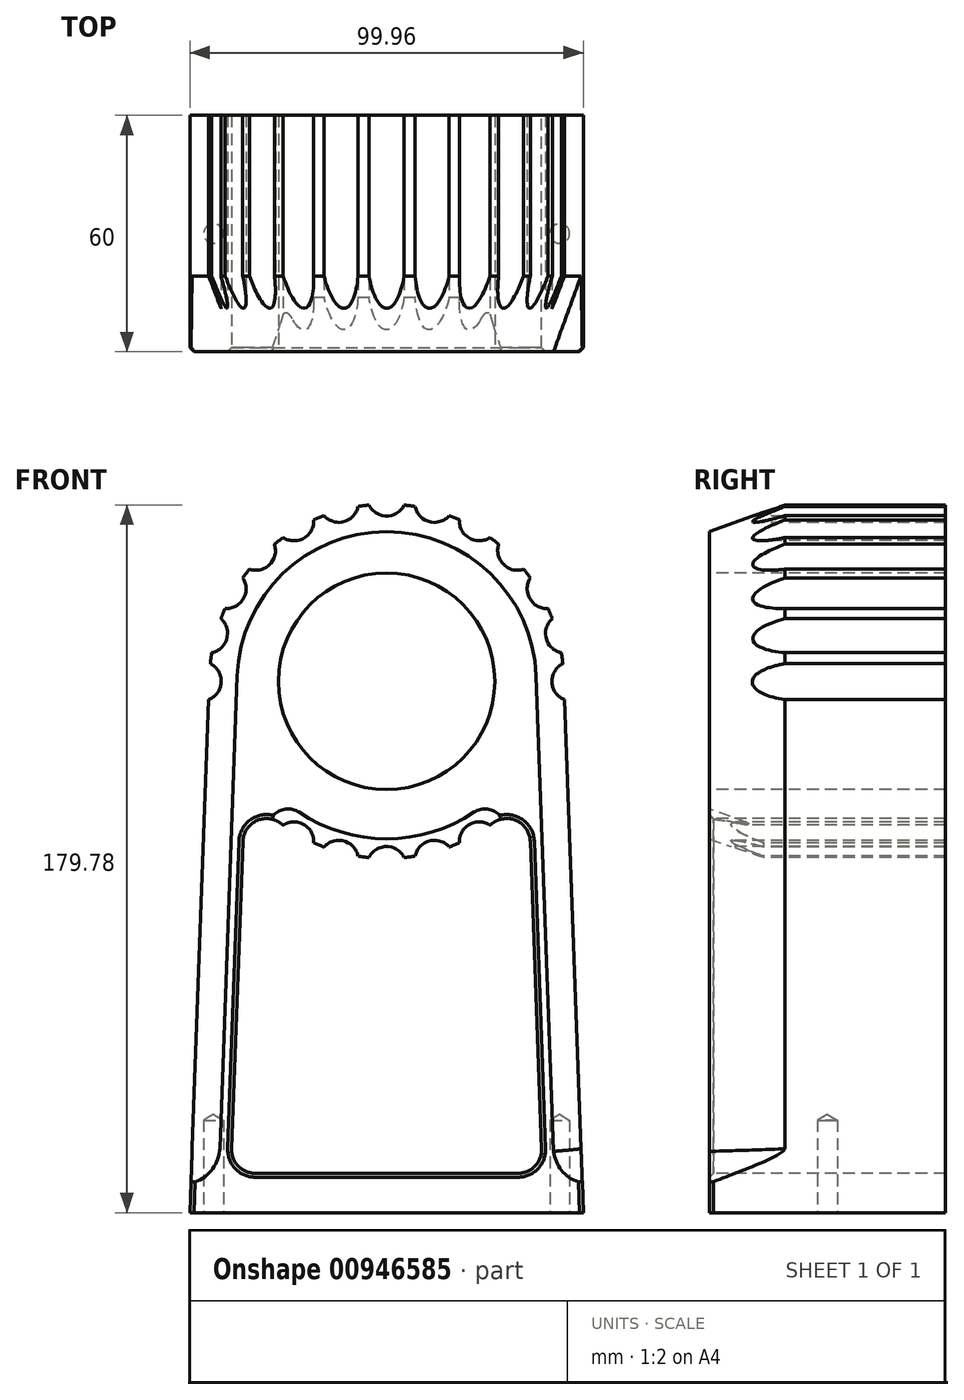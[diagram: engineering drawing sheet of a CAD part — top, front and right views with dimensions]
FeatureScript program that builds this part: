
annotation { "Feature Type Name" : "Feature", "Feature Type Description" : "" }
export const myFeature = defineFeature(function(context is Context, id is Id, definition is map)
    precondition{}
    {
        {
            var Q0;
            Q0=qCreatedBy(makeId("Front.planeOp"),FACE);
            var sketch = newSketch(context, id + "F0", { "sketchPlane" : qUnion([Q0])});
            skLineSegment(sketch, "E0.top", {"start": v(-50, -99.3) * mm, "end": v(-49.96, -99.3) * mm});
            skLineSegment(sketch, "E1", {"start": v(0, 121.96) * mm, "end": v(0, -115.93) * mm, "construction": true});
            skCircle(sketch, "E2", {"center": v(0, 35.7) * mm, "radius": 27.5 * mm});
            skLineSegment(sketch, "E3.trimOffspring", {"start": v(-39.59, -89.3) * mm, "end": v(39.63, -89.3) * mm});
            skPoint(sketch, "E4.orphan", {"position": v(-49.96, -99.3) * mm});
            skLineSegment(sketch, "E5", {"start": v(-68.26, 80.7) * mm, "end": v(50, 80.7) * mm, "construction": true});
            skLineSegment(sketch, "E6", {"start": v(50, 80.7) * mm, "end": v(50, -149.68) * mm, "construction": true});
            skArc(sketch, "E7", {"start": v(44.97, 37.36) * mm, "mid": v(0, 80.7) * mm, "end": v(-44.97, 37.34) * mm});
            skLineSegment(sketch, "E8", {"start": v(-49.96, -99.3) * mm, "end": v(-44.97, 37.34) * mm});
            skLineSegment(sketch, "E9", {"start": v(50, -99.3) * mm, "end": v(44.97, 37.36) * mm});
            skArc(sketch, "E10.trimOffspring", {"start": v(-36, 8.71) * mm, "mid": v(0, -9.3) * mm, "end": v(36.02, 8.72) * mm});
            skLineSegment(sketch, "E11.trimOffspring", {"start": v(39.63, -89.3) * mm, "end": v(36.02, 8.72) * mm});
            skLineSegment(sketch, "E12.trimOffspring", {"start": v(-39.59, -89.3) * mm, "end": v(-36, 8.71) * mm});
            skLineSegment(sketch, "E13.trimOffspring", {"start": v(-49.96, -99.3) * mm, "end": v(50, -99.3) * mm});
            skSolve(sketch);
        }
        {
            var Q0;
            Q0=qSketchRegion(id+"F0",true);
            extrude(context, id + "F1", {"entities" : qUnion([Q0]), "oppositeDirection" : true, "depth" : 60 * mm, "offsetDistance" : 25 * mm});
        }
        {
            var Q0;
            Q0=makeQuery(id+"F1.opExtrude","CAP_FACE",FACE,{"disambiguationData":[OSD([sQuery(id+"F0.wireOp",EDGE,"E2"),sQuery(id+"F0.wireOp",EDGE,"E3.trimOffspring"),sQuery(id+"F0.wireOp",EDGE,"E7"),sQuery(id+"F0.wireOp",EDGE,"E8"),sQuery(id+"F0.wireOp",EDGE,"E9"),sQuery(id+"F0.wireOp",EDGE,"E10.trimOffspring"),sQuery(id+"F0.wireOp",EDGE,"E11.trimOffspring"),sQuery(id+"F0.wireOp",EDGE,"E12.trimOffspring"),sQuery(id+"F0.wireOp",EDGE,"E13.trimOffspring")])],"isStart":true});
            var sketch = newSketch(context, id + "F2", { "sketchPlane" : qUnion([Q0])});
            skArc(sketch, "E14.0", {"start": v(44.97, 37.36) * mm, "mid": v(0, 80.7) * mm, "end": v(-44.97, 37.34) * mm, "construction": true});
            skArc(sketch, "E15.0", {"start": v(61.97, 55.33) * mm, "mid": v(0, 100.7) * mm, "end": v(-61.97, 55.33) * mm});
            skArc(sketch, "E16.0", {"start": v(37.97, 37.1) * mm, "mid": v(0, 73.7) * mm, "end": v(-37.97, 37.09) * mm});
            skArc(sketch, "E17.0", {"start": v(-36, 8.71) * mm, "mid": v(0, -9.3) * mm, "end": v(36.02, 8.72) * mm, "construction": true});
            skArc(sketch, "E18.0", {"start": v(-22.22, 2.44) * mm, "mid": v(0, -4.3) * mm, "end": v(22.22, 2.44) * mm});
            skArc(sketch, "E19.0", {"start": v(-21.86, -25.51) * mm, "mid": v(0.68, -29.3) * mm, "end": v(23.14, -25.04) * mm});
            skArc(sketch, "E20", {"start": v(-22.22, 2.44) * mm, "mid": v(-28.07, 2.23) * mm, "end": v(-29.71, -3.39) * mm});
            skArc(sketch, "E21", {"start": v(29.78, -3.17) * mm, "mid": v(27.98, 2.3) * mm, "end": v(22.22, 2.44) * mm});
            skLineSegment(sketch, "E22", {"start": v(-21.86, -25.51) * mm, "end": v(-29.71, -3.39) * mm});
            skLineSegment(sketch, "E23", {"start": v(23.14, -25.04) * mm, "end": v(29.78, -3.17) * mm});
            skLineSegment(sketch, "E24", {"start": v(0, 35.7) * mm, "end": v(0, -65.78) * mm, "construction": true});
            skLineSegment(sketch, "E25", {"start": v(-37.97, 37.09) * mm, "end": v(-42.36, -82.91) * mm});
            skLineSegment(sketch, "E26", {"start": v(37.97, 37.1) * mm, "end": v(42.42, -83.72) * mm});
            skArc(sketch, "E27", {"start": v(-49.69, -91.8) * mm, "mid": v(-44.52, -88.6) * mm, "end": v(-42.36, -82.91) * mm});
            skArc(sketch, "E28.MirrorCS", {"start": v(49.69, -91.8) * mm, "mid": v(44.78, -88.9) * mm, "end": v(42.42, -83.72) * mm});
            skLineSegment(sketch, "E29", {"start": v(-61.97, 55.33) * mm, "end": v(-94.94, -91.8) * mm});
            skLineSegment(sketch, "E30", {"start": v(-94.94, -91.8) * mm, "end": v(-49.69, -91.8) * mm});
            skLineSegment(sketch, "E31.MirrorCS", {"start": v(61.97, 55.33) * mm, "end": v(94.94, -91.8) * mm});
            skLineSegment(sketch, "E32.MirrorCS", {"start": v(94.94, -91.8) * mm, "end": v(49.69, -91.8) * mm});
            skSolve(sketch);
        }
        {
            var Q0;
            {var subQ0=sQuery(id+"F2.wireOp",EDGE,"E18.0");Q0=makeQuery(id+"F2.imprint","IMPRINT",FACE,{"disambiguationData":[TD([[makeQuery(id+"F2.imprint","IMPRINT",EDGE,{"derivedFrom":subQ0}),-1.0]])]});}
            var Q1;
            Q1=makeQuery(id+"F2.imprint","IMPRINT",FACE,{"disambiguationData":[TD([[makeQuery(id+"F2.imprint","IMPRINT",EDGE,{"derivedFrom":sQuery(id+"F2.wireOp",EDGE,"E19.0")}),1.0]])]});
            var Q2;
            Q2=makeQuery(id+"F2.imprint","IMPRINT",FACE,{"disambiguationData":[TD([[makeQuery(id+"F2.imprint","IMPRINT",EDGE,{"derivedFrom":sQuery(id+"F2.wireOp",EDGE,"E15.0")}),1.0]])]});
            var Q3;
            Q3=makeQuery(id+"F2.imprint","IMPRINT",FACE,{"disambiguationData":[TD([[makeQuery(id+"F2.imprint","IMPRINT",EDGE,{"derivedFrom":sQuery(id+"F2.wireOp",EDGE,"E16.0")}),-1.0]])]});
            extrude(context, id + "F3", {"entities" : qUnion([Q0, Q1, Q2, Q3]), "operationType" : NewBodyOperationType.REMOVE, "endBound" : BoundingType.THROUGH_ALL, "oppositeDirection" : true, "depth" : 25 * mm, "offsetDistance" : 25 * mm, "hasDraft" : true, "draftAngle" : 20 * degree, "draftPullDirection" : true});
        }
        {
            var Q0;
            Q0=makeQuery(id+"F1.opExtrude","SWEPT_EDGE",EDGE,{"disambiguationData":[OSD([sQuery(id+"F0.wireOp",EDGE,"E10.trimOffspring"),sQuery(id+"F0.wireOp",EDGE,"E12.trimOffspring")])]});
            var Q1;
            Q1=makeQuery(id+"F1.opExtrude","SWEPT_EDGE",EDGE,{"disambiguationData":[OSD([sQuery(id+"F0.wireOp",EDGE,"E10.trimOffspring"),sQuery(id+"F0.wireOp",EDGE,"E11.trimOffspring")])]});
            var Q2;
            Q2=makeQuery(id+"F1.opExtrude","SWEPT_EDGE",EDGE,{"disambiguationData":[OSD([sQuery(id+"F0.wireOp",EDGE,"E3.trimOffspring"),sQuery(id+"F0.wireOp",EDGE,"E12.trimOffspring")])]});
            var Q3;
            Q3=makeQuery(id+"F1.opExtrude","SWEPT_EDGE",EDGE,{"disambiguationData":[OSD([sQuery(id+"F0.wireOp",EDGE,"E3.trimOffspring"),sQuery(id+"F0.wireOp",EDGE,"E11.trimOffspring")])]});
            fillet(context, id + "F4", {"entities" : qUnion([Q0, Q1, Q2, Q3]), "radius" : 6 * mm, "tangentPropagation" : true, "allowEdgeOverflow" : false});
        }
        {
            var Q0;
            Q0=makeQuery(id+"F1.opExtrude","CAP_FACE",FACE,{"disambiguationData":[OSD([sQuery(id+"F0.wireOp",EDGE,"E2"),sQuery(id+"F0.wireOp",EDGE,"E3.trimOffspring"),sQuery(id+"F0.wireOp",EDGE,"E7"),sQuery(id+"F0.wireOp",EDGE,"E8"),sQuery(id+"F0.wireOp",EDGE,"E9"),sQuery(id+"F0.wireOp",EDGE,"E10.trimOffspring"),sQuery(id+"F0.wireOp",EDGE,"E11.trimOffspring"),sQuery(id+"F0.wireOp",EDGE,"E12.trimOffspring"),sQuery(id+"F0.wireOp",EDGE,"E13.trimOffspring")])],"isStart":true});
            var sketch = newSketch(context, id + "F5", { "sketchPlane" : qUnion([Q0])});
            skArc(sketch, "E33", {"start": v(-44.4, 42.96) * mm, "mid": v(-44.62, 41.58) * mm, "end": v(-44.78, 40.18) * mm});
            skLineSegment(sketch, "E34", {"start": v(0, 35.7) * mm, "end": v(0, 109) * mm, "construction": true});
            skPoint(sketch, "E35", {"position": v(0, 82.7) * mm});
            skLineSegment(sketch, "E36.anchor1", {"start": v(0, 35.7) * mm, "end": v(0, 82.7) * mm, "construction": true});
            skLineSegment(sketch, "E36.anchor2", {"start": v(0, 35.7) * mm, "end": v(0, 82.7) * mm, "construction": true});
            skArc(sketch, "E37", {"start": v(-4.48, 80.48) * mm, "mid": v(0, 77.7) * mm, "end": v(4.48, 80.48) * mm});
            skArc(sketch, "E38.1.0", {"start": v(-15.91, 77.8) * mm, "mid": v(-10.87, 76.27) * mm, "end": v(-7.26, 80.11) * mm});
            skArc(sketch, "E38.2.0", {"start": v(-26.27, 72.24) * mm, "mid": v(-21, 72.07) * mm, "end": v(-18.5, 76.72) * mm});
            skArc(sketch, "E38.3.0", {"start": v(-34.83, 64.2) * mm, "mid": v(-29.7, 65.4) * mm, "end": v(-28.5, 70.53) * mm});
            skArc(sketch, "E38.4.0", {"start": v(-41.02, 54.21) * mm, "mid": v(-36.37, 56.7) * mm, "end": v(-36.54, 61.97) * mm});
            skArc(sketch, "E38.5.0", {"start": v(-44.4, 42.96) * mm, "mid": v(-40.57, 46.57) * mm, "end": v(-42.1, 51.62) * mm});
            skArc(sketch, "E38.6.0", {"start": v(-46.73, 30.7) * mm, "mid": v(-42.1, 34.69) * mm, "end": v(-44.78, 40.18) * mm});
            skArc(sketch, "E38.10.0", {"start": v(-18.5, -5.32) * mm, "mid": v(-21.93, -0.26) * mm, "end": v(-27.7, -2.27) * mm});
            skArc(sketch, "E38.11.0", {"start": v(-7.26, -8.7) * mm, "mid": v(-10.87, -4.87) * mm, "end": v(-15.91, -6.4) * mm});
            skArc(sketch, "E38.12.0", {"start": v(4.48, -9.08) * mm, "mid": v(0, -6.3) * mm, "end": v(-4.48, -9.08) * mm});
            skArc(sketch, "E38.13.0", {"start": v(15.91, -6.4) * mm, "mid": v(10.87, -4.87) * mm, "end": v(7.26, -8.7) * mm});
            skArc(sketch, "E38.14.0", {"start": v(27.7, -2.27) * mm, "mid": v(21.93, -0.26) * mm, "end": v(18.5, -5.32) * mm});
            skArc(sketch, "E38.18.0", {"start": v(44.78, 40.18) * mm, "mid": v(42.1, 34.69) * mm, "end": v(46.73, 30.7) * mm});
            skArc(sketch, "E38.19.0", {"start": v(42.1, 51.62) * mm, "mid": v(40.57, 46.57) * mm, "end": v(44.4, 42.96) * mm});
            skArc(sketch, "E38.21.0", {"start": v(28.5, 70.53) * mm, "mid": v(29.7, 65.4) * mm, "end": v(34.83, 64.2) * mm});
            skArc(sketch, "E38.22.0", {"start": v(18.5, 76.72) * mm, "mid": v(21, 72.07) * mm, "end": v(26.27, 72.24) * mm});
            skArc(sketch, "E38.23.0", {"start": v(7.26, 80.11) * mm, "mid": v(10.87, 76.27) * mm, "end": v(15.91, 77.8) * mm});
            skArc(sketch, "E39", {"start": v(46.73, 30.7) * mm, "mid": v(0, 82.7) * mm, "end": v(-46.73, 30.7) * mm});
            skArc(sketch, "E40.trimOffspring", {"start": v(-41.02, 54.21) * mm, "mid": v(-41.57, 52.92) * mm, "end": v(-42.1, 51.62) * mm});
            skArc(sketch, "E41.trimOffspring", {"start": v(-34.83, 64.2) * mm, "mid": v(-35.7, 63.1) * mm, "end": v(-36.54, 61.97) * mm});
            skArc(sketch, "E42.trimOffspring", {"start": v(-26.27, 72.24) * mm, "mid": v(-27.4, 71.4) * mm, "end": v(-28.5, 70.53) * mm});
            skArc(sketch, "E43.trimOffspring", {"start": v(-15.91, 77.8) * mm, "mid": v(-17.22, 77.28) * mm, "end": v(-18.5, 76.72) * mm});
            skArc(sketch, "E44.trimOffspring", {"start": v(-4.48, 80.48) * mm, "mid": v(-5.87, 80.32) * mm, "end": v(-7.26, 80.11) * mm});
            skArc(sketch, "E45.trimOffspring", {"start": v(18.5, 76.72) * mm, "mid": v(11.65, 79.17) * mm, "end": v(4.48, 80.48) * mm});
            skArc(sketch, "E46.trimOffspring", {"start": v(28.5, 70.53) * mm, "mid": v(27.4, 71.4) * mm, "end": v(26.27, 72.24) * mm});
            skArc(sketch, "E47.trimOffspring", {"start": v(36.54, 61.97) * mm, "mid": v(35.7, 63.1) * mm, "end": v(34.83, 64.2) * mm});
            skArc(sketch, "E48.trimOffspring", {"start": v(42.1, 51.62) * mm, "mid": v(41.57, 52.92) * mm, "end": v(41.02, 54.21) * mm});
            skArc(sketch, "E49.trimOffspring", {"start": v(36.54, 61.97) * mm, "mid": v(36.37, 56.7) * mm, "end": v(41.02, 54.21) * mm});
            skArc(sketch, "E50.trimOffspring", {"start": v(44.78, 40.18) * mm, "mid": v(44.62, 41.58) * mm, "end": v(44.4, 42.96) * mm});
            skArc(sketch, "E51.trimOffspring", {"start": v(-27.7, -2.27) * mm, "mid": v(0, -11.3) * mm, "end": v(27.7, -2.27) * mm});
            skArc(sketch, "E52.trimOffspring", {"start": v(-18.5, -5.32) * mm, "mid": v(-17.22, -5.87) * mm, "end": v(-15.91, -6.4) * mm});
            skArc(sketch, "E53.trimOffspring", {"start": v(15.91, -6.4) * mm, "mid": v(17.22, -5.87) * mm, "end": v(18.5, -5.32) * mm});
            skArc(sketch, "E54.trimOffspring", {"start": v(4.48, -9.08) * mm, "mid": v(5.87, -8.91) * mm, "end": v(7.26, -8.7) * mm});
            skArc(sketch, "E55.trimOffspring", {"start": v(-7.26, -8.7) * mm, "mid": v(-5.87, -8.91) * mm, "end": v(-4.48, -9.08) * mm});
            skSolve(sketch);
        }
        {
            var Q0;
            Q0 = qSketchRegion(id + "F5", true);
            extrude(context, id + "F6", {"entities" : qUnion([Q0]), "operationType" : NewBodyOperationType.REMOVE, "endBound" : BoundingType.THROUGH_ALL, "oppositeDirection" : true, "depth" : 25 * mm, "offsetDistance" : 25 * mm});
        }
        {
            var Q0;
            Q0=makeQuery(id+"F1.opExtrude","SWEPT_FACE",FACE,{"disambiguationData":[OSD([sQuery(id+"F0.wireOp",EDGE,"E13.trimOffspring")])]});
            var sketch = newSketch(context, id + "F7", { "sketchPlane" : qUnion([Q0])});
            skPoint(sketch, "E56", {"position": v(-25, -12.5) * mm});
            skPoint(sketch, "E57.0.1.0", {"position": v(-25, -47.5) * mm});
            skPoint(sketch, "E57.1.0.0", {"position": v(25, -12.5) * mm});
            skPoint(sketch, "E57.1.1.0", {"position": v(25, -47.5) * mm});
            skLineSegment(sketch, "E57.direction1", {"start": v(-25, -12.5) * mm, "end": v(25, -12.5) * mm, "construction": true});
            skLineSegment(sketch, "E57.direction2", {"start": v(-25, -12.5) * mm, "end": v(-25, -47.5) * mm, "construction": true});
            skPoint(sketch, "E58", {"position": v(-43.96, -30) * mm});
            skPoint(sketch, "E58.positionSnap0", {"position": v(-25, -30) * mm});
            skPoint(sketch, "E59", {"position": v(44, -30) * mm});
            skPoint(sketch, "E59.positionSnap0", {"position": v(50, -30) * mm});
            skSolve(sketch);
        }
        {
            var Q0;
            Q0=sQuery(id+"F7.wireOp",VERTEX,"E59");
            var Q1;
            Q1=sQuery(id+"F7.wireOp",VERTEX,"E58");
            var Q2;
            Q2=makeQuery(id+"F1.opExtrude","SWEPT_BODY",BODY,{"disambiguationData":[OSD([sQuery(id+"F0.wireOp",EDGE,"E0.top"),sQuery(id+"F0.wireOp",EDGE,"E2"),sQuery(id+"F0.wireOp",EDGE,"xHJD9Emc-sb2g-noab-fFY3-X2ls41XAQOft"),sQuery(id+"F0.wireOp",EDGE,"rRfU7ory-cBGn-840H-I0kd-4tql2qusLkEy"),sQuery(id+"F0.wireOp",EDGE,"babb2c87-e115-43c3-b4c8-a2120738efa6.0"),sQuery(id+"F0.wireOp",EDGE,"d8799dad-38b5-4738-9c1e-a39866b82842.0"),sQuery(id+"F0.wireOp",EDGE,"JPpXpM9p-0zDs-tQAe-tmeS-4BvX9Xfdr4c8"),sQuery(id+"F0.wireOp",EDGE,"262e45c6-1378-4927-a352-d10a1b2b0039.trimOffspring"),sQuery(id+"F0.wireOp",EDGE,"E3.trimOffspring"),sQuery(id+"F0.wireOp",EDGE,"00b187a7-d7e1-4cdd-ae0b-6ea0999bff0c.filletArc"),sQuery(id+"F0.wireOp",EDGE,"e7ac8887-ac85-4bfc-9bda-0ffc56bab970.filletArc")])]});
            hole(context, id + "F8", {"style" : HoleStyle.SIMPLE, "endStyle" : HoleEndStyle.BLIND, "standardTappedOrClearance" : lookupTablePath({ "standard" : "ISO", "engagement" : "75%", "pitch" : "1 mm", "size" : "M6", "type" : "Tapped" }), "standardBlindInLast" : lookupTablePath({ "standard" : "ISO", "fit" : "Normal", "engagement" : "75%", "pitch" : "1 mm", "size" : "M6", "type" : "Clearance & tapped" }), "holeDiameter" : 5 * mm, "majorDiameter" : 6 * mm, "showTappedDepth" : true, "holeDepth" : 23.5 * mm, "isTappedThrough" : true, "tappedDepth" : 20.5 * mm, "tapClearance" : 3, "locations" : qUnion([Q0, Q1]), "scope" : qUnion([Q2])});
        }
        {
            var Q0;
            Q0=makeQuery(id+"F1.opExtrude","CAP_EDGE",EDGE,{"disambiguationData":[OSD([sQuery(id+"F0.wireOp",EDGE,"E11.trimOffspring")])],"isStart":true});
            var Q1;
            Q1=makeQuery(id+"F1.opExtrude","CAP_EDGE",EDGE,{"disambiguationData":[OSD([sQuery(id+"F0.wireOp",EDGE,"E9")])],"isStart":true});
            var Q2;
            Q2=makeQuery(id+"F1.opExtrude","CAP_EDGE",EDGE,{"disambiguationData":[OSD([sQuery(id+"F0.wireOp",EDGE,"E8")])],"isStart":true});
            chamfer(context, id + "F9", {"entities" : qUnion([Q0, Q1, Q2]), "width" : 1 * mm, "tangentPropagation" : true});
        }
    });
